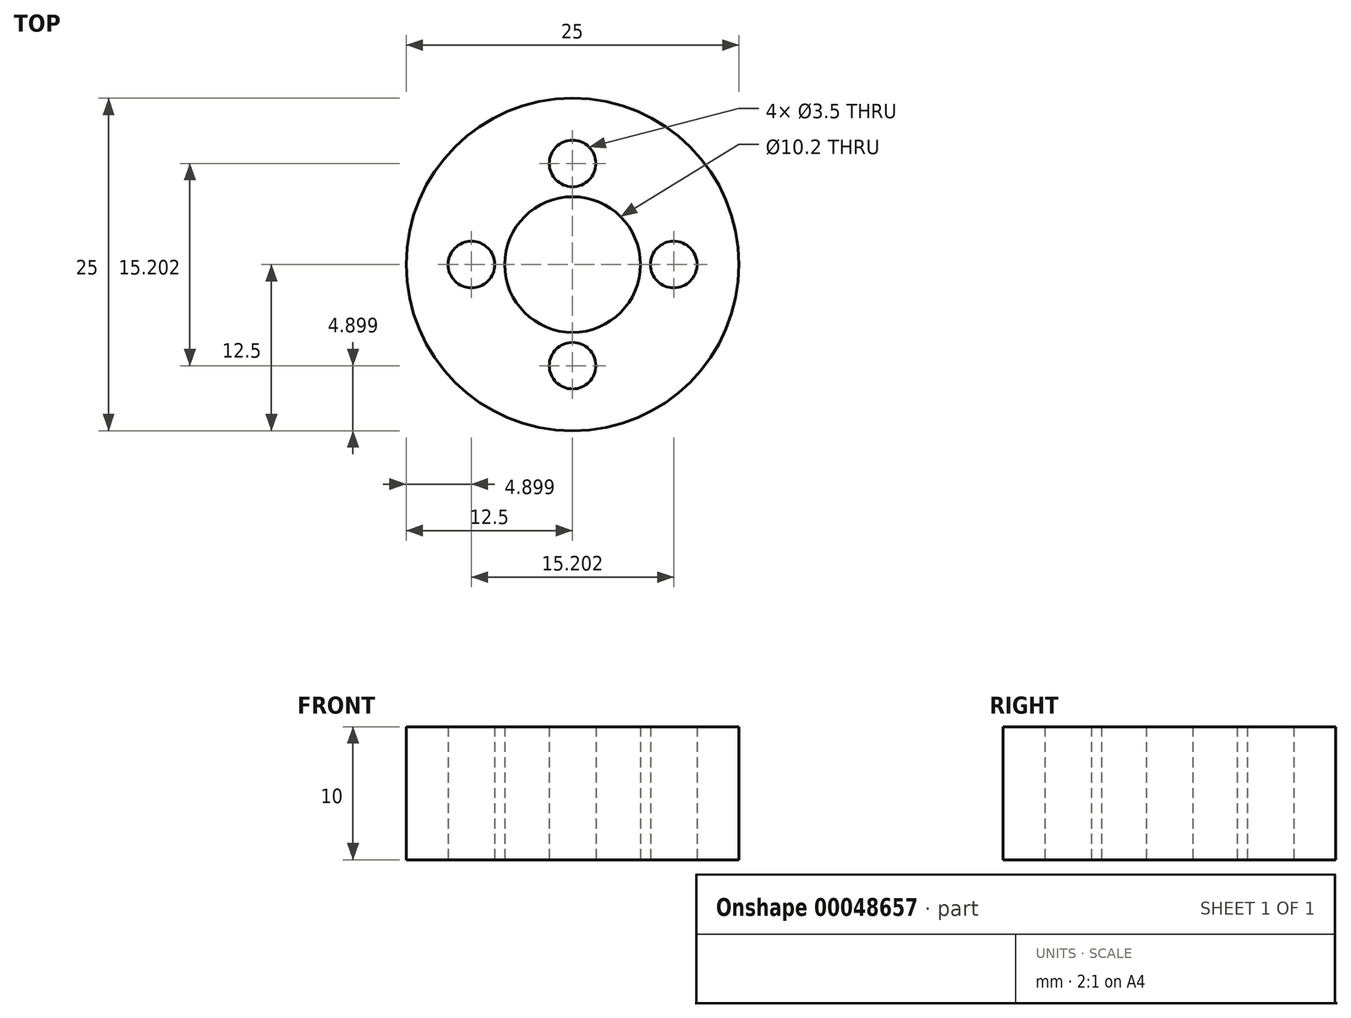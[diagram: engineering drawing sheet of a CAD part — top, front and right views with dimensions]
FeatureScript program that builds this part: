
annotation { "Feature Type Name" : "Feature", "Feature Type Description" : "" }
export const myFeature = defineFeature(function(context is Context, id is Id, definition is map)
    precondition{}
    {
        {
            var Q0;
            Q0=qCreatedBy(makeId("Top.planeOp"),FACE);
            var sketch = newSketch(context, id + "F0", { "sketchPlane" : qUnion([Q0])});
            skCircle(sketch, "E0", {"center": v(0, 0) * mm, "radius": 12.5 * mm});
            skCircle(sketch, "E1", {"center": v(0, 0) * mm, "radius": 5.1 * mm});
            skCircle(sketch, "E2", {"center": v(0, 7.6) * mm, "radius": 1.75 * mm});
            skCircle(sketch, "E3.1.0", {"center": v(-7.6, 0) * mm, "radius": 1.75 * mm});
            skCircle(sketch, "E3.2.0", {"center": v(0, -7.6) * mm, "radius": 1.75 * mm});
            skCircle(sketch, "E3.3.0", {"center": v(7.6, 0) * mm, "radius": 1.75 * mm});
            skSolve(sketch);
        }
        {
            var Q0;
            Q0=makeQuery(id+"F0.imprint","IMPRINT",FACE,{"disambiguationData":[TD([[makeQuery(id+"F0.imprint","IMPRINT",EDGE,{"derivedFrom":sQuery(id+"F0.wireOp",EDGE,"E0")}),1.0]])]});
            extrude(context, id + "F1", {"entities" : qUnion([Q0]), "depth" : 10 * mm});
        }
    });
